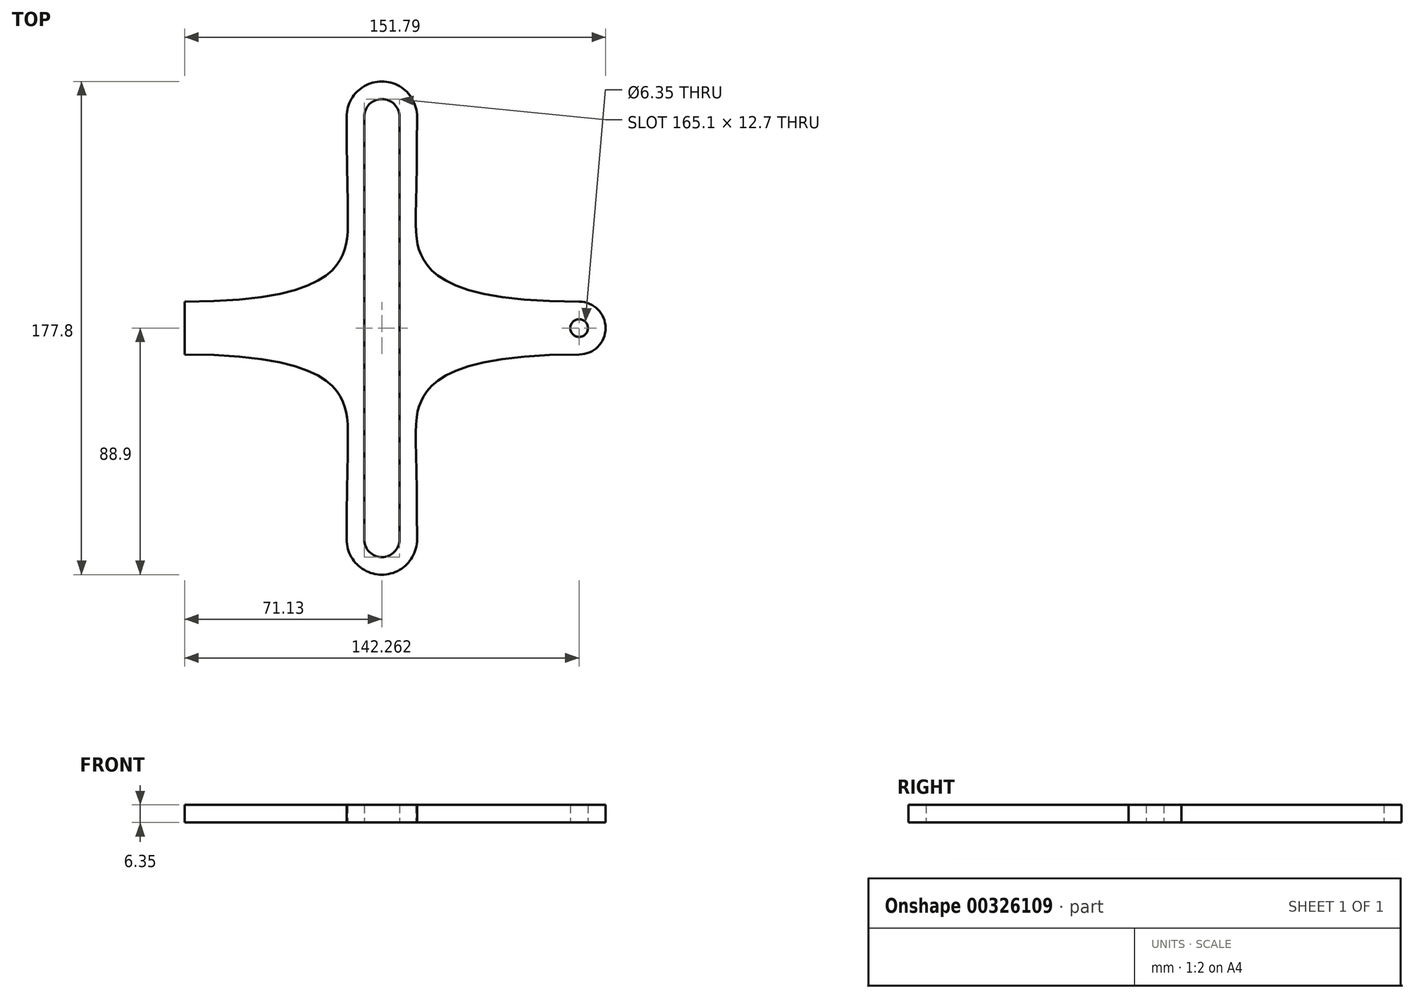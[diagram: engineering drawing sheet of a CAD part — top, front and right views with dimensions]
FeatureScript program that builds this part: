
annotation { "Feature Type Name" : "Feature", "Feature Type Description" : "" }
export const myFeature = defineFeature(function(context is Context, id is Id, definition is map)
    precondition{}
    {
        {
            var Q0;
            Q0=qCreatedBy(makeId("Top.planeOp"),FACE);
            var sketch = newSketch(context, id + "F0", { "sketchPlane" : qUnion([Q0])});
            skArc(sketch, "E0", {"start": v(6.35, 76.2) * mm, "mid": v(0, 82.55) * mm, "end": v(-6.35, 76.2) * mm});
            skArc(sketch, "E1.0", {"start": v(12.7, 76.18) * mm, "mid": v(0, 88.9) * mm, "end": v(-12.7, 76.18) * mm});
            skArc(sketch, "E2.MirrorC", {"start": v(12.7, -76.18) * mm, "mid": v(0, -88.9) * mm, "end": v(-12.7, -76.18) * mm});
            skArc(sketch, "E3.MirrorC", {"start": v(6.35, -76.2) * mm, "mid": v(0, -82.55) * mm, "end": v(-6.35, -76.2) * mm});
            skCircle(sketch, "E4", {"center": v(71.13, 0) * mm, "radius": 3.18 * mm});
            skArc(sketch, "E5", {"start": v(71.13, -9.53) * mm, "mid": v(80.66, 0) * mm, "end": v(71.13, 9.53) * mm});
            skFitSpline(sketch, "E6", {"points": [v(12.7, 76.18) * mm, v(14.05, 26.62) * mm, v(71.13, 9.53) * mm], "startDerivative": vector(-0.46, -242.55) * mm, "endDerivative": vector(261.28, 0) * mm});
            skFitSpline(sketch, "E7.MirrorCS", {"points": [v(12.7, -76.18) * mm, v(14.05, -26.62) * mm, v(71.13, -9.53) * mm], "startDerivative": vector(-0.46, 242.55) * mm, "endDerivative": vector(261.28, 0) * mm});
            skFitSpline(sketch, "E8.MirrorCS", {"points": [v(-12.7, 76.18) * mm, v(-14.05, 26.62) * mm, v(-71.13, 9.53) * mm], "startDerivative": vector(0.46, -242.55) * mm, "endDerivative": vector(-261.28, 0) * mm});
            skFitSpline(sketch, "E9.MirrorCS", {"points": [v(-12.7, -76.18) * mm, v(-14.05, -26.62) * mm, v(-71.13, -9.53) * mm], "startDerivative": vector(0.46, 242.55) * mm, "endDerivative": vector(-261.28, 0) * mm});
            skLineSegment(sketch, "E10", {"start": v(-71.13, 9.52) * mm, "end": v(-71.13, -9.52) * mm});
            skLineSegment(sketch, "E11", {"start": v(-6.35, 76.2) * mm, "end": v(-6.35, -76.2) * mm});
            skLineSegment(sketch, "E12", {"start": v(6.35, -76.2) * mm, "end": v(6.35, 76.2) * mm});
            skPoint(sketch, "E13.start.orphan", {"position": v(0, 9.53) * mm});
            skSolve(sketch);
        }
        {
            var Q0;
            Q0 = qSketchRegion(id + "F0", true);
            extrude(context, id + "F1", {"entities" : qUnion([Q0]), "depth" : 6.35 * mm});
        }
    });
